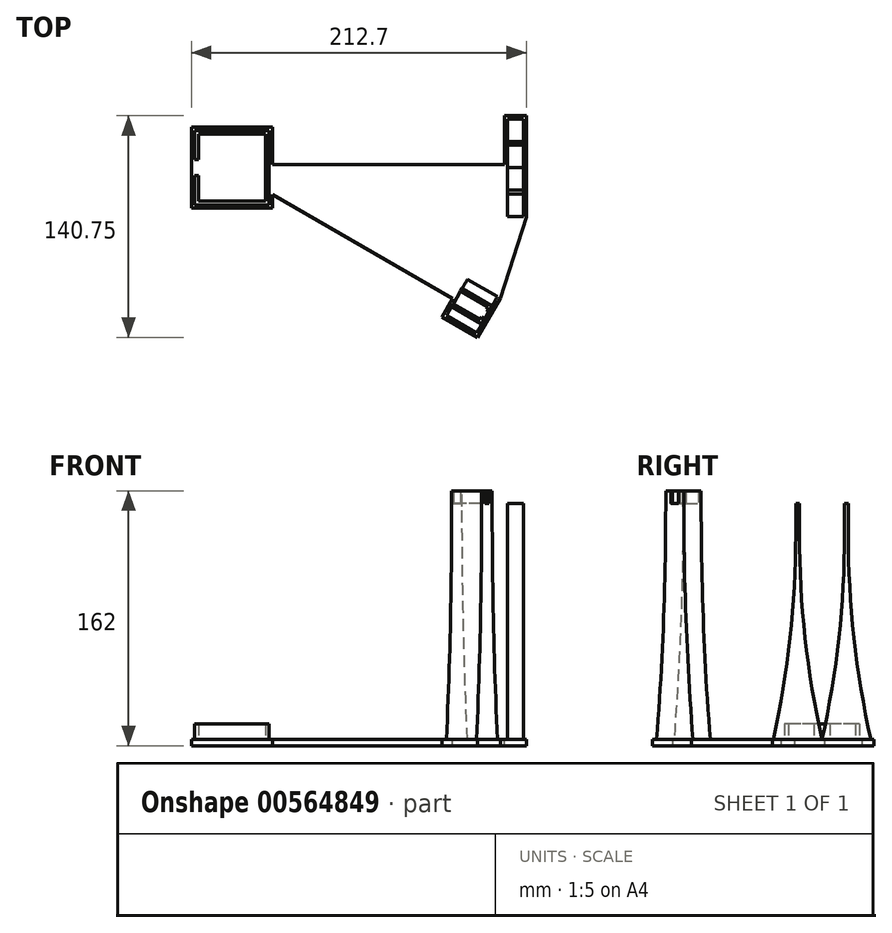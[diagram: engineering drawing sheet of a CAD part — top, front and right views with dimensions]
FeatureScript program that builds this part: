
annotation { "Feature Type Name" : "Feature", "Feature Type Description" : "" }
export const myFeature = defineFeature(function(context is Context, id is Id, definition is map)
    precondition{}
    {
        {
            var Q0;
            Q0=qCreatedBy(makeId("Top.planeOp"),FACE);
            var sketch = newSketch(context, id + "F0", { "sketchPlane" : qUnion([Q0])});
            skLineSegment(sketch, "E0.bottom", {"start": v(21.2, 21.2) * mm, "end": v(-21.2, 21.2) * mm});
            skLineSegment(sketch, "E0.top", {"start": v(21.2, -21.2) * mm, "end": v(-21.2, -21.2) * mm});
            skLineSegment(sketch, "E0.left", {"start": v(21.2, 21.2) * mm, "end": v(21.2, -21.2) * mm});
            skLineSegment(sketch, "E0.right", {"start": v(-21.2, 21.2) * mm, "end": v(-21.2, -21.2) * mm});
            skPoint(sketch, "E0.middle", {"position": v(0, 0) * mm});
            skLineSegment(sketch, "E1.bottom", {"start": v(23.7, 23.7) * mm, "end": v(-23.7, 23.7) * mm});
            skLineSegment(sketch, "E1.top", {"start": v(23.7, -23.7) * mm, "end": v(-23.7, -23.7) * mm});
            skLineSegment(sketch, "E1.left", {"start": v(23.7, 23.7) * mm, "end": v(23.7, -23.7) * mm});
            skLineSegment(sketch, "E1.right", {"start": v(-23.7, 23.7) * mm, "end": v(-23.7, -23.7) * mm});
            skLineSegment(sketch, "E2", {"start": v(0, 0) * mm, "end": v(-23.7, 0) * mm});
            skLineSegment(sketch, "E3", {"start": v(-23.7, 0) * mm, "end": v(-23.7, -5) * mm});
            skLineSegment(sketch, "E4", {"start": v(-23.7, -5) * mm, "end": v(-21.2, -5) * mm});
            skLineSegment(sketch, "E5", {"start": v(-21.2, -5) * mm, "end": v(-21.2, 5) * mm});
            skLineSegment(sketch, "E6.bottom", {"start": v(-21.2, 5) * mm, "end": v(-23.7, 5) * mm});
            skLineSegment(sketch, "E6.top", {"start": v(-21.2, -5) * mm, "end": v(-23.7, -5) * mm});
            skLineSegment(sketch, "E6.left", {"start": v(-21.2, 5) * mm, "end": v(-21.2, -5) * mm});
            skLineSegment(sketch, "E6.right", {"start": v(-23.7, 5) * mm, "end": v(-23.7, -5) * mm});
            skSolve(sketch);
        }
        {
            var Q0;
            {var subQ9=sQuery(id+"F0.wireOp",EDGE,"E0.bottom");Q0=makeQuery(id+"F0.imprint","IMPRINT",FACE,{"disambiguationData":[TD([[makeQuery(id+"F0.imprint","IMPRINT",EDGE,{"derivedFrom":subQ9}),-1.0]])]});}
            extrude(context, id + "F1", {"entities" : qUnion([Q0]), "depth" : 10 * mm, "offsetDistance" : 25 * mm});
        }
        {
            var Q0;
            Q0=qCreatedBy(makeId("Top.planeOp"),FACE);
            var sketch = newSketch(context, id + "F2", { "sketchPlane" : qUnion([Q0])});
            skLineSegment(sketch, "E7", {"start": v(0, 0) * mm, "end": v(175, 0) * mm});
            skSolve(sketch);
        }
        {
            var Q0;
            Q0=sQuery(id+"F2.wireOp",VERTEX,"E7.end");
            var Q1;
            Q1=sQuery(id+"F2.wireOp",EDGE,"E7");
            cPlane(context, id + "F3", {"entities" : qUnion([Q0, Q1]), "cplaneType" : CPlaneType.CURVE_POINT, "offset" : 25 * mm, "width" : 150 * mm, "height" : 150 * mm});
        }
        {
            var Q0;
            Q0=qCreatedBy(id+"F3.planeOp",FACE);
            var sketch = newSketch(context, id + "F4", { "sketchPlane" : qUnion([Q0])});
            skLineSegment(sketch, "E8", {"start": v(0, 0) * mm, "end": v(15.5, 0) * mm});
            skLineSegment(sketch, "E9", {"start": v(15.5, 0) * mm, "end": v(-15.5, 0) * mm});
            skLineSegment(sketch, "E10", {"start": v(-15.5, 0) * mm, "end": v(-15.5, 150) * mm});
            skLineSegment(sketch, "E11", {"start": v(-15.5, 150) * mm, "end": v(-15.5, 130) * mm});
            skLineSegment(sketch, "E12", {"start": v(-15.5, 150) * mm, "end": v(-14.3, 150) * mm});
            skLineSegment(sketch, "E13", {"start": v(-14.3, 150) * mm, "end": v(-16.7, 150) * mm});
            skLineSegment(sketch, "E14", {"start": v(-16.7, 150) * mm, "end": v(-16.7, 130) * mm});
            skLineSegment(sketch, "E15.top", {"start": v(-14.3, 130) * mm, "end": v(-16.7, 130) * mm});
            skLineSegment(sketch, "E15.left", {"start": v(-14.3, 150) * mm, "end": v(-14.3, 130) * mm});
            skArc(sketch, "E16", {"start": v(-14.3, 130) * mm, "mid": v(-10.71, 64.6) * mm, "end": v(0, 0) * mm});
            skLineSegment(sketch, "E17", {"start": v(-15.5, 0) * mm, "end": v(-31, 0) * mm});
            skArc(sketch, "E18", {"start": v(-16.7, 130) * mm, "mid": v(-20.29, 64.6) * mm, "end": v(-31, 0) * mm});
            skLineSegment(sketch, "E19", {"start": v(0, 0) * mm, "end": v(0, 200) * mm});
            skLineSegment(sketch, "E20.MirrorCS", {"start": v(15.5, 150) * mm, "end": v(15.5, 130) * mm});
            skLineSegment(sketch, "E21.MirrorCS", {"start": v(15.5, 0) * mm, "end": v(15.5, 150) * mm});
            skArc(sketch, "E22.MirrorCS", {"start": v(16.7, 130) * mm, "mid": v(20.29, 64.6) * mm, "end": v(31, 0) * mm});
            skLineSegment(sketch, "E23.MirrorCS", {"start": v(16.7, 150) * mm, "end": v(16.7, 130) * mm});
            skLineSegment(sketch, "E24.MirrorCS", {"start": v(14.3, 150) * mm, "end": v(14.3, 130) * mm});
            skArc(sketch, "E25.MirrorCS", {"start": v(14.3, 130) * mm, "mid": v(10.71, 64.6) * mm, "end": v(0, 0) * mm});
            skLineSegment(sketch, "E26.MirrorCS", {"start": v(14.3, 150) * mm, "end": v(16.7, 150) * mm});
            skLineSegment(sketch, "E27.MirrorCS", {"start": v(15.5, 0) * mm, "end": v(31, 0) * mm});
            skSolve(sketch);
        }
        {
            var Q0;
            Q0=makeQuery(id+"F4.imprint","IMPRINT",FACE,{"disambiguationData":[TD([[makeQuery(id+"F4.imprint","IMPRINT",EDGE,{"derivedFrom":sQuery(id+"F4.wireOp",EDGE,"E22.MirrorCS")}),-1.0]])]});
            var Q1;
            {var subQ0=sQuery(id+"F4.wireOp",EDGE,"E24.MirrorCS");Q1=makeQuery(id+"F4.imprint","IMPRINT",FACE,{"disambiguationData":[TD([[makeQuery(id+"F4.imprint","IMPRINT",EDGE,{"derivedFrom":subQ0}),1.0]])]});}
            var Q2;
            {var subQ0=sQuery(id+"F4.wireOp",EDGE,"E10");Q2=makeQuery(id+"F4.imprint","IMPRINT",FACE,{"disambiguationData":[TD([[makeQuery(id+"F4.imprint","IMPRINT",EDGE,{"derivedFrom":subQ0}),-1.0]])]});}
            var Q3;
            {var subQ0=sQuery(id+"F4.wireOp",EDGE,"E10");Q3=makeQuery(id+"F4.imprint","IMPRINT",FACE,{"disambiguationData":[TD([[makeQuery(id+"F4.imprint","IMPRINT",EDGE,{"derivedFrom":subQ0}),1.0]])]});}
            var Q4;
            {var subQ0=sQuery(id+"F4.wireOp",EDGE,"E11");Q4=makeQuery(id+"F4.imprint","IMPRINT",FACE,{"disambiguationData":[TD([[makeQuery(id+"F4.imprint","IMPRINT",EDGE,{"derivedFrom":subQ0}),1.0]])]});}
            var Q5;
            {var subQ0=sQuery(id+"F4.wireOp",EDGE,"E11");Q5=makeQuery(id+"F4.imprint","IMPRINT",FACE,{"disambiguationData":[TD([[makeQuery(id+"F4.imprint","IMPRINT",EDGE,{"derivedFrom":subQ0}),-1.0]])]});}
            extrude(context, id + "F5", {"entities" : qUnion([Q0, Q1, Q2, Q3, Q4, Q5]), "depth" : 10 * mm, "offsetDistance" : 25 * mm});
        }
        {
            var Q0;
            Q0=qCreatedBy(makeId("Right.planeOp"),FACE);
            var sketch = newSketch(context, id + "F6", { "sketchPlane" : qUnion([Q0])});
            skLineSegment(sketch, "E28", {"start": v(0, 0) * mm, "end": v(0, 100) * mm});
            skSolve(sketch);
        }
        {
            var Q0;
            Q0=sQuery(id+"F2.wireOp",EDGE,"E7");
            var Q1;
            Q1=sQuery(id+"F6.wireOp",EDGE,"E28");
            revolve(context, id + "F7", {"bodyType" : ToolBodyType.SURFACE, "surfaceEntities" : qUnion([Q0]), "axis" : qUnion([Q1]), "revolveType" : RevolveType.ONE_DIRECTION, "oppositeDirection" : true, "angle" : 30 * degree});
        }
        {
            var Q0;
            Q0=makeQuery(id+"F7.opRevolve","CAP_VERTEX",VERTEX,{"disambiguationData":[OSD([sQuery(id+"F2.wireOp",VERTEX,"E7.end")])],"isStart":false});
            var Q1;
            Q1=makeQuery(id+"F7.opRevolve","CAP_EDGE",EDGE,{"disambiguationData":[OSD([sQuery(id+"F2.wireOp",EDGE,"E7")])],"isStart":false});
            cPlane(context, id + "F8", {"entities" : qUnion([Q0, Q1]), "cplaneType" : CPlaneType.CURVE_POINT, "offset" : 25 * mm, "width" : 150 * mm, "height" : 150 * mm});
        }
        {
            var Q0;
            Q0=qCreatedBy(id+"F8.planeOp",FACE);
            var sketch = newSketch(context, id + "F9", { "sketchPlane" : qUnion([Q0])});
            skLineSegment(sketch, "E29", {"start": v(0, 0) * mm, "end": v(0, 150) * mm});
            skSolve(sketch);
        }
        {
            var Q0;
            Q0=sQuery(id+"F9.wireOp",VERTEX,"E29.end");
            var Q1;
            Q1=sQuery(id+"F9.wireOp",EDGE,"E29");
            cPlane(context, id + "F10", {"entities" : qUnion([Q0, Q1]), "cplaneType" : CPlaneType.CURVE_POINT, "offset" : 25 * mm, "width" : 150 * mm, "height" : 150 * mm});
        }
        {
            var Q0;
            Q0=qCreatedBy(id+"F10.planeOp",FACE);
            var sketch = newSketch(context, id + "F11", { "sketchPlane" : qUnion([Q0])});
            skPoint(sketch, "E30.0", {"position": v(151.55, -87.5) * mm});
            skLineSegment(sketch, "E31.bottom", {"start": v(161.55, -82.85) * mm, "end": v(141.55, -82.85) * mm});
            skLineSegment(sketch, "E31.top", {"start": v(161.55, -92.15) * mm, "end": v(141.55, -92.15) * mm});
            skLineSegment(sketch, "E31.left", {"start": v(161.55, -82.85) * mm, "end": v(161.55, -92.15) * mm});
            skLineSegment(sketch, "E31.right", {"start": v(141.55, -82.85) * mm, "end": v(141.55, -92.15) * mm});
            skLineSegment(sketch, "E32.0", {"start": v(163.55, -80.85) * mm, "end": v(141.55, -80.85) * mm});
            skLineSegment(sketch, "E32.1", {"start": v(163.55, -80.85) * mm, "end": v(163.55, -94.15) * mm});
            skLineSegment(sketch, "E32.2", {"start": v(163.55, -94.15) * mm, "end": v(141.55, -94.15) * mm});
            skLineSegment(sketch, "E33", {"start": v(141.55, -80.85) * mm, "end": v(141.55, -82.85) * mm});
            skLineSegment(sketch, "E34", {"start": v(141.55, -92.15) * mm, "end": v(141.55, -94.15) * mm});
            skLineSegment(sketch, "E35", {"start": v(161.55, -87.5) * mm, "end": v(163.55, -87.5) * mm});
            skLineSegment(sketch, "E36.bottom", {"start": v(163.55, -84.8) * mm, "end": v(161.55, -84.8) * mm});
            skLineSegment(sketch, "E36.top", {"start": v(163.55, -90.2) * mm, "end": v(161.55, -90.2) * mm});
            skLineSegment(sketch, "E36.left", {"start": v(163.55, -84.8) * mm, "end": v(163.55, -90.2) * mm});
            skLineSegment(sketch, "E36.right", {"start": v(161.55, -84.8) * mm, "end": v(161.55, -90.2) * mm});
            skPoint(sketch, "E36.middle", {"position": v(162.55, -87.5) * mm});
            skSolve(sketch);
        }
        {
            var Q0;
            {var subQ4=sQuery(id+"F11.wireOp",EDGE,"E31.bottom");Q0=makeQuery(id+"F11.imprint","IMPRINT",FACE,{"disambiguationData":[TD([[makeQuery(id+"F11.imprint","IMPRINT",EDGE,{"derivedFrom":subQ4}),-1.0]])]});}
            var Q1;
            {var subQ4=sQuery(id+"F11.wireOp",EDGE,"E31.top");Q1=makeQuery(id+"F11.imprint","IMPRINT",FACE,{"disambiguationData":[TD([[makeQuery(id+"F11.imprint","IMPRINT",EDGE,{"derivedFrom":subQ4}),1.0]])]});}
            extrude(context, id + "F12", {"entities" : qUnion([Q0, Q1]), "depth" : 8 * mm, "offsetDistance" : 25 * mm});
        }
        {
            var Q0;
            Q0=qCreatedBy(id+"F10.planeOp",FACE);
            var sketch = newSketch(context, id + "F13", { "sketchPlane" : qUnion([Q0])});
            skPoint(sketch, "E37.0", {"position": v(163.55, -94.15) * mm});
            skPoint(sketch, "E38.0", {"position": v(141.55, -80.85) * mm});
            skLineSegment(sketch, "E39.bottom", {"start": v(163.55, -94.15) * mm, "end": v(141.55, -94.15) * mm});
            skLineSegment(sketch, "E39.top", {"start": v(163.55, -80.85) * mm, "end": v(141.55, -80.85) * mm});
            skLineSegment(sketch, "E39.left", {"start": v(163.55, -94.15) * mm, "end": v(163.55, -80.85) * mm});
            skLineSegment(sketch, "E39.right", {"start": v(141.55, -94.15) * mm, "end": v(141.55, -80.85) * mm});
            skSolve(sketch);
        }
        {
            var Q0;
            Q0=makeQuery(id+"F13.imprint","IMPRINT",FACE,{"disambiguationData":[TD([[makeQuery(id+"F13.imprint","IMPRINT",EDGE,{"derivedFrom":sQuery(id+"F13.wireOp",EDGE,"E39.bottom")}),-1.0]])]});
            extrude(context, id + "F14", {"entities" : qUnion([Q0]), "oppositeDirection" : true, "depth" : 2 * mm, "offsetDistance" : 25 * mm});
        }
        {
            var Q0;
            Q0=makeQuery(id+"F14.opExtrude","CAP_EDGE",EDGE,{"disambiguationData":[OSD([sQuery(id+"F13.wireOp",EDGE,"E39.bottom")])],"isStart":false});
            var Q1;
            Q1=makeQuery(id+"F14.opExtrude","CAP_VERTEX",VERTEX,{"disambiguationData":[OSD([sQuery(id+"F13.wireOp",EDGE,"E39.bottom"),sQuery(id+"F13.wireOp",EDGE,"E39.left")])],"isStart":false});
            cPlane(context, id + "F15", {"entities" : qUnion([Q0, Q1]), "cplaneType" : CPlaneType.CURVE_POINT, "offset" : 25 * mm, "width" : 150 * mm, "height" : 150 * mm});
        }
        {
            var Q0;
            Q0=qCreatedBy(id+"F15.planeOp",FACE);
            var sketch = newSketch(context, id + "F16", { "sketchPlane" : qUnion([Q0])});
            skPoint(sketch, "E40.0", {"position": v(87.5, 148) * mm});
            skLineSegment(sketch, "E41", {"start": v(87.5, 148) * mm, "end": v(87.5, 0) * mm});
            skLineSegment(sketch, "E42", {"start": v(87.5, 0) * mm, "end": v(100.8, 0) * mm});
            skLineSegment(sketch, "E43", {"start": v(100.8, 0) * mm, "end": v(74.2, 0) * mm});
            skPoint(sketch, "E44.0", {"position": v(80.85, 148) * mm});
            skLineSegment(sketch, "E45.0", {"start": v(80.85, 148) * mm, "end": v(80.85, 150) * mm});
            skLineSegment(sketch, "E46.0", {"start": v(94.15, 148) * mm, "end": v(94.15, 150) * mm});
            skPoint(sketch, "E47.0", {"position": v(94.15, 148) * mm});
            skArc(sketch, "E48", {"start": v(80.85, 148) * mm, "mid": v(79.19, 73.93) * mm, "end": v(74.2, 0) * mm});
            skArc(sketch, "E49", {"start": v(94.15, 148) * mm, "mid": v(95.81, 73.93) * mm, "end": v(100.8, 0) * mm});
            skLineSegment(sketch, "E50", {"start": v(80.85, 148) * mm, "end": v(94.15, 148) * mm});
            skSolve(sketch);
        }
        {
            var Q0;
            {var subQ0=sQuery(id+"F16.wireOp",EDGE,"E41");Q0=makeQuery(id+"F16.imprint","IMPRINT",FACE,{"disambiguationData":[TD([[makeQuery(id+"F16.imprint","IMPRINT",EDGE,{"derivedFrom":subQ0}),-1.0]])]});}
            var Q1;
            {var subQ0=sQuery(id+"F16.wireOp",EDGE,"E41");Q1=makeQuery(id+"F16.imprint","IMPRINT",FACE,{"disambiguationData":[TD([[makeQuery(id+"F16.imprint","IMPRINT",EDGE,{"derivedFrom":subQ0}),1.0]])]});}
            extrude(context, id + "F17", {"entities" : qUnion([Q0, Q1]), "operationType" : NewBodyOperationType.ADD, "depth" : 22 * mm, "offsetDistance" : 25 * mm});
        }
        {
            var Q0;
            Q0=makeQuery(id+"F14.opExtrude","SWEPT_BODY",BODY,{"disambiguationData":[OSD([sQuery(id+"F13.wireOp",EDGE,"E39.bottom"),sQuery(id+"F13.wireOp",EDGE,"E39.top"),sQuery(id+"F13.wireOp",EDGE,"E39.left"),sQuery(id+"F13.wireOp",EDGE,"E39.right")])]});
            var Q1;
            Q1=makeQuery(id+"F12.opExtrude","SWEPT_BODY",BODY,{"disambiguationData":[OSD([sQuery(id+"F11.wireOp",EDGE,"E31.top"),sQuery(id+"F11.wireOp",EDGE,"E31.left"),sQuery(id+"F11.wireOp",EDGE,"E32.1"),sQuery(id+"F11.wireOp",EDGE,"E32.2"),sQuery(id+"F11.wireOp",EDGE,"E34"),sQuery(id+"F11.wireOp",EDGE,"E36.top")])]});
            var Q2;
            Q2=makeQuery(id+"F12.opExtrude","SWEPT_BODY",BODY,{"disambiguationData":[OSD([sQuery(id+"F11.wireOp",EDGE,"E31.bottom"),sQuery(id+"F11.wireOp",EDGE,"E31.left"),sQuery(id+"F11.wireOp",EDGE,"E32.0"),sQuery(id+"F11.wireOp",EDGE,"E32.1"),sQuery(id+"F11.wireOp",EDGE,"E33"),sQuery(id+"F11.wireOp",EDGE,"E36.bottom")])]});
            booleanBodies(context, id + "F18", {"operationType" : BooleanOperationType.UNION, "tools" : qUnion([Q0, Q1, Q2])});
        }
        {
            var Q0;
            Q0=makeQuery(id+"F14.opExtrude","SWEPT_BODY",BODY,{"disambiguationData":[OSD([sQuery(id+"F13.wireOp",EDGE,"E39.bottom"),sQuery(id+"F13.wireOp",EDGE,"E39.top"),sQuery(id+"F13.wireOp",EDGE,"E39.left"),sQuery(id+"F13.wireOp",EDGE,"E39.right")])]});
            var Q1;
            Q1=sQuery(id+"F9.wireOp",EDGE,"E29");
            transform(context, id + "F19", {"entities" : qUnion([Q0]), "transformType" : TransformType.ROTATION, "transformAxis" : qUnion([Q1]), "angle" : 30 * degree, "oppositeDirection" : true, "makeCopy" : false});
        }
        {
            var Q0;
            Q0=qCreatedBy(makeId("Top.planeOp"),FACE);
            var sketch = newSketch(context, id + "F20", { "sketchPlane" : qUnion([Q0])});
            skPoint(sketch, "E51.0", {"position": v(-23.7, -23.7) * mm});
            skPoint(sketch, "E52.0", {"position": v(23.7, 23.7) * mm});
            skPoint(sketch, "E53.0", {"position": v(23.7, 0) * mm});
            skLineSegment(sketch, "E54.0", {"start": v(175, 0) * mm, "end": v(175, 31) * mm});
            skLineSegment(sketch, "E55.0", {"start": v(185, 31) * mm, "end": v(175, 31) * mm});
            skLineSegment(sketch, "E56.0", {"start": v(185, 0) * mm, "end": v(185, 31) * mm});
            skLineSegment(sketch, "E57.0", {"start": v(185, 0) * mm, "end": v(185, -31) * mm});
            skLineSegment(sketch, "E58.0", {"start": v(155.3, -105.02) * mm, "end": v(168.6, -81.98) * mm});
            skLineSegment(sketch, "E59.0", {"start": v(136.24, -94.02) * mm, "end": v(155.3, -105.02) * mm});
            skArc(sketch, "E60.0.2", {"start": v(175, 0) * mm, "mid": v(169.04, -45.3) * mm, "end": v(151.55, -87.5) * mm});
            skLineSegment(sketch, "E61.bottom", {"start": v(-23.7, -23.7) * mm, "end": v(23.7, -23.7) * mm});
            skLineSegment(sketch, "E61.top", {"start": v(-23.7, 23.7) * mm, "end": v(23.7, 23.7) * mm});
            skLineSegment(sketch, "E61.left", {"start": v(-23.7, -23.7) * mm, "end": v(-23.7, 23.7) * mm});
            skLineSegment(sketch, "E62", {"start": v(23.7, -13.68) * mm, "end": v(23.7, -23.7) * mm});
            skLineSegment(sketch, "E63", {"start": v(23.7, 0) * mm, "end": v(23.7, 23.7) * mm});
            skLineSegment(sketch, "E64", {"start": v(23.7, -13.68) * mm, "end": v(142.9, -82.5) * mm});
            skLineSegment(sketch, "E65", {"start": v(142.9, -82.5) * mm, "end": v(136.24, -94.02) * mm});
            skLineSegment(sketch, "E66", {"start": v(175, 0) * mm, "end": v(23.7, 0) * mm});
            skLineSegment(sketch, "E67", {"start": v(168.6, -81.98) * mm, "end": v(185, -31) * mm});
            skLineSegment(sketch, "E68.0", {"start": v(-25.7, -25.7) * mm, "end": v(-25.7, 25.7) * mm});
            skLineSegment(sketch, "E68.1", {"start": v(-25.7, 25.7) * mm, "end": v(25.7, 25.7) * mm});
            skLineSegment(sketch, "E68.2", {"start": v(25.7, 2) * mm, "end": v(25.7, 25.7) * mm});
            skLineSegment(sketch, "E68.3", {"start": v(173, 2) * mm, "end": v(25.7, 2) * mm});
            skLineSegment(sketch, "E68.4", {"start": v(133.51, -94.75) * mm, "end": v(156.03, -107.75) * mm});
            skLineSegment(sketch, "E68.5", {"start": v(140.16, -83.23) * mm, "end": v(133.51, -94.75) * mm});
            skLineSegment(sketch, "E68.6", {"start": v(25.7, -17.15) * mm, "end": v(140.16, -83.23) * mm});
            skLineSegment(sketch, "E68.7", {"start": v(25.7, -17.15) * mm, "end": v(25.7, -25.7) * mm});
            skLineSegment(sketch, "E68.8", {"start": v(156.03, -107.75) * mm, "end": v(170.44, -82.8) * mm});
            skLineSegment(sketch, "E68.9", {"start": v(170.44, -82.8) * mm, "end": v(187, -31.31) * mm});
            skLineSegment(sketch, "E68.10", {"start": v(187, 0) * mm, "end": v(187, -31.31) * mm});
            skLineSegment(sketch, "E68.11", {"start": v(187, 0) * mm, "end": v(187, 33) * mm});
            skLineSegment(sketch, "E68.12", {"start": v(-25.7, -25.7) * mm, "end": v(25.7, -25.7) * mm});
            skLineSegment(sketch, "E68.13", {"start": v(187, 33) * mm, "end": v(173, 33) * mm});
            skLineSegment(sketch, "E68.14", {"start": v(173, 2) * mm, "end": v(173, 33) * mm});
            skSolve(sketch);
        }
        {
            var Q0;
            Q0=makeQuery(id+"F20.imprint","IMPRINT",FACE,{"disambiguationData":[TD([[makeQuery(id+"F20.imprint","IMPRINT",EDGE,{"derivedFrom":sQuery(id+"F20.wireOp",EDGE,"E54.0")}),1.0]])]});
            var Q1;
            Q1=makeQuery(id+"F20.imprint","IMPRINT",FACE,{"disambiguationData":[TD([[makeQuery(id+"F20.imprint","IMPRINT",EDGE,{"derivedFrom":sQuery(id+"F20.wireOp",EDGE,"E54.0")}),-1.0]])]});
            extrude(context, id + "F21", {"entities" : qUnion([Q0, Q1]), "oppositeDirection" : true, "depth" : 4 * mm, "offsetDistance" : 25 * mm});
        }
    });
